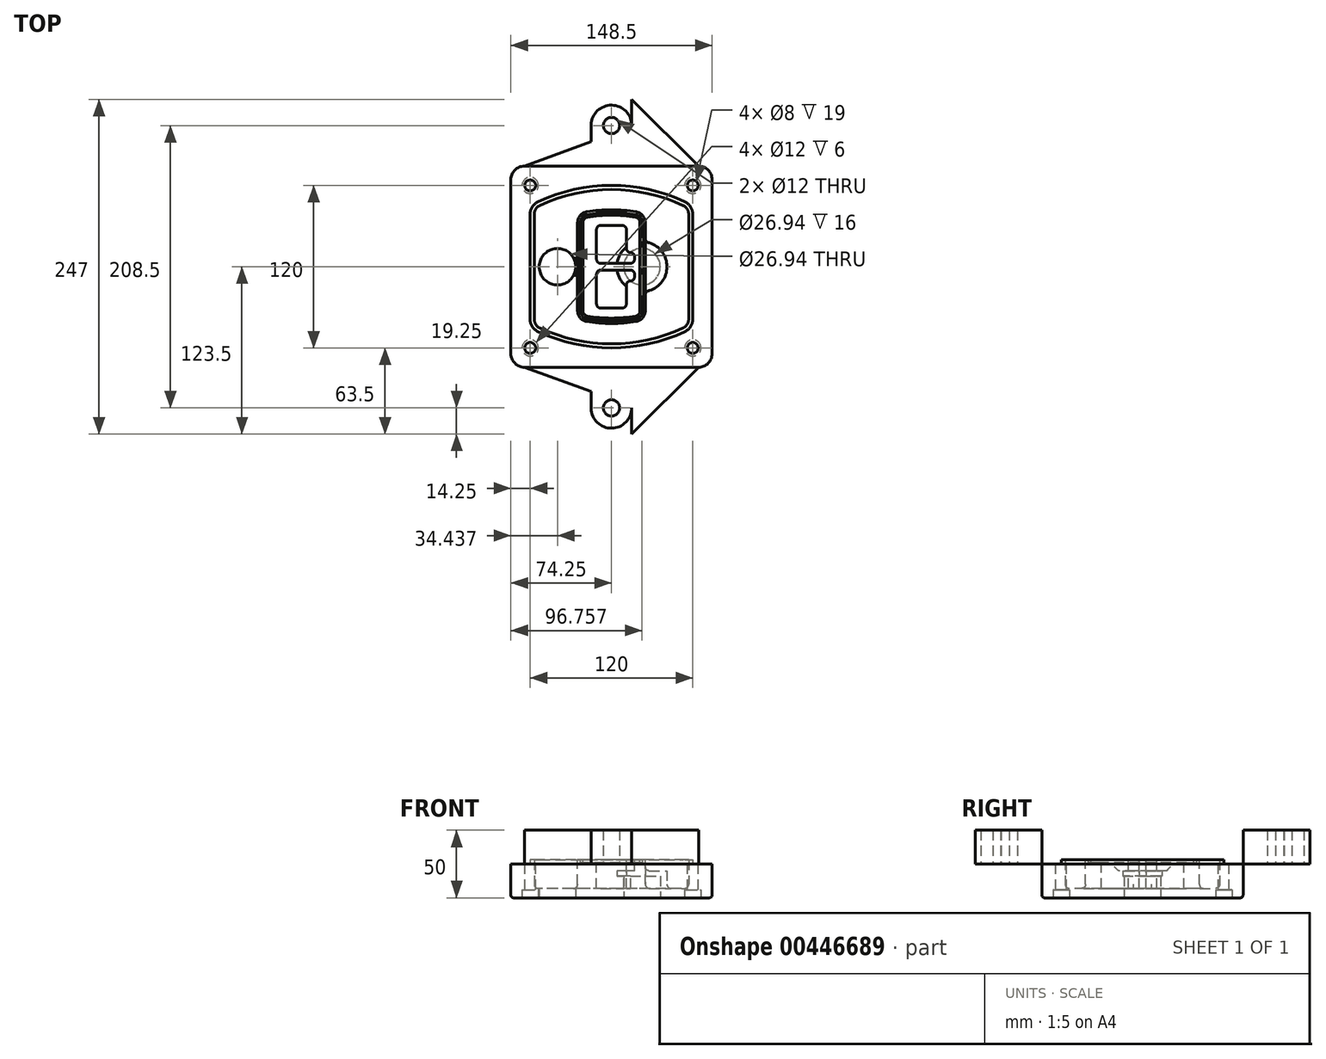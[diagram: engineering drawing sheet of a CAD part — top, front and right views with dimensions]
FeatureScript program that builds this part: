
annotation { "Feature Type Name" : "Feature", "Feature Type Description" : "" }
export const myFeature = defineFeature(function(context is Context, id is Id, definition is map)
    precondition{}
    {
        {
            var Q0;
            Q0=qCreatedBy(makeId("Top.planeOp"),FACE);
            var sketch = newSketch(context, id + "F0", { "sketchPlane" : qUnion([Q0])});
            skPoint(sketch, "E0.rect.middle", {"position": v(0, 0) * mm});
            skLineSegment(sketch, "E1.bottom", {"start": v(-64.25, -74.25) * mm, "end": v(64.25, -74.25) * mm});
            skLineSegment(sketch, "E1.top", {"start": v(-64.25, 74.25) * mm, "end": v(64.25, 74.25) * mm});
            skLineSegment(sketch, "E1.left", {"start": v(-74.25, -64.25) * mm, "end": v(-74.25, 64.25) * mm});
            skLineSegment(sketch, "E1.right", {"start": v(74.25, -64.25) * mm, "end": v(74.25, 64.25) * mm});
            skLineSegment(sketch, "E2", {"start": v(-74.25, 74.25) * mm, "end": v(74.25, -74.25) * mm, "construction": true});
            skLineSegment(sketch, "E3", {"start": v(74.25, 74.25) * mm, "end": v(-74.25, -74.25) * mm, "construction": true});
            skCircle(sketch, "E4", {"center": v(-60, 60) * mm, "radius": 4 * mm});
            skCircle(sketch, "E5", {"center": v(60, 60) * mm, "radius": 4 * mm});
            skCircle(sketch, "E6", {"center": v(60, -60) * mm, "radius": 4 * mm});
            skCircle(sketch, "E7", {"center": v(-60, -60) * mm, "radius": 4 * mm});
            skLineSegment(sketch, "E8", {"start": v(-60, 60) * mm, "end": v(60, 60) * mm, "construction": true});
            skLineSegment(sketch, "E9", {"start": v(60, 60) * mm, "end": v(60, -60) * mm, "construction": true});
            skLineSegment(sketch, "E10", {"start": v(60, -60) * mm, "end": v(-60, -60) * mm, "construction": true});
            skLineSegment(sketch, "E11", {"start": v(-60, -60) * mm, "end": v(-60, 60) * mm, "construction": true});
            skLineSegment(sketch, "E12", {"start": v(-60, 38.83) * mm, "end": v(-60, -38.83) * mm});
            skLineSegment(sketch, "E13", {"start": v(60, 38.83) * mm, "end": v(60, -38.83) * mm});
            skArc(sketch, "E14", {"start": v(54.26, 47.88) * mm, "mid": v(0, 60) * mm, "end": v(-54.26, 47.88) * mm});
            skArc(sketch, "E15", {"start": v(-54.26, -47.88) * mm, "mid": v(0, -60) * mm, "end": v(54.26, -47.88) * mm});
            skLineSegment(sketch, "E16", {"start": v(-60, 0) * mm, "end": v(60, 0) * mm, "construction": true});
            skPoint(sketch, "E17.visualSharp", {"position": v(-60, -45) * mm});
            skArc(sketch, "E17.filletArc", {"start": v(-60, -38.83) * mm, "mid": v(-58.44, -44.2) * mm, "end": v(-54.26, -47.88) * mm});
            skPoint(sketch, "E18.visualSharp", {"position": v(-60, 45) * mm});
            skArc(sketch, "E18.filletArc", {"start": v(-54.26, 47.88) * mm, "mid": v(-58.44, 44.2) * mm, "end": v(-60, 38.83) * mm});
            skPoint(sketch, "E19.visualSharp", {"position": v(60, 45) * mm});
            skArc(sketch, "E19.filletArc", {"start": v(60, 38.83) * mm, "mid": v(58.44, 44.2) * mm, "end": v(54.26, 47.88) * mm});
            skPoint(sketch, "E20.visualSharp", {"position": v(60, -45) * mm});
            skArc(sketch, "E20.filletArc", {"start": v(54.26, -47.88) * mm, "mid": v(58.44, -44.2) * mm, "end": v(60, -38.83) * mm});
            skPoint(sketch, "E21.visualSharp", {"position": v(-74.25, 74.25) * mm});
            skArc(sketch, "E21.filletArc", {"start": v(-64.25, 74.25) * mm, "mid": v(-71.32, 71.32) * mm, "end": v(-74.25, 64.25) * mm});
            skPoint(sketch, "E22.visualSharp", {"position": v(74.25, 74.25) * mm});
            skArc(sketch, "E22.filletArc", {"start": v(74.25, 64.25) * mm, "mid": v(71.32, 71.32) * mm, "end": v(64.25, 74.25) * mm});
            skPoint(sketch, "E23.visualSharp", {"position": v(74.25, -74.25) * mm});
            skArc(sketch, "E23.filletArc", {"start": v(64.25, -74.25) * mm, "mid": v(71.32, -71.32) * mm, "end": v(74.25, -64.25) * mm});
            skPoint(sketch, "E24.visualSharp", {"position": v(-74.25, -74.25) * mm});
            skArc(sketch, "E24.filletArc", {"start": v(-74.25, -64.25) * mm, "mid": v(-71.32, -71.32) * mm, "end": v(-64.25, -74.25) * mm});
            skArc(sketch, "E25.0", {"start": v(57, 38.83) * mm, "mid": v(55.9, 42.58) * mm, "end": v(52.98, 45.17) * mm});
            skLineSegment(sketch, "E25.1", {"start": v(57, 38.83) * mm, "end": v(57, -38.83) * mm});
            skArc(sketch, "E25.2", {"start": v(52.98, -45.17) * mm, "mid": v(55.9, -42.58) * mm, "end": v(57, -38.83) * mm});
            skArc(sketch, "E25.3", {"start": v(-52.98, -45.17) * mm, "mid": v(0, -57) * mm, "end": v(52.98, -45.17) * mm});
            skArc(sketch, "E25.4", {"start": v(-57, -38.83) * mm, "mid": v(-55.9, -42.58) * mm, "end": v(-52.98, -45.17) * mm});
            skArc(sketch, "E25.5", {"start": v(52.98, 45.17) * mm, "mid": v(0, 57) * mm, "end": v(-52.98, 45.17) * mm});
            skLineSegment(sketch, "E25.6", {"start": v(-57, 38.83) * mm, "end": v(-57, -38.83) * mm});
            skArc(sketch, "E25.7", {"start": v(-52.98, 45.17) * mm, "mid": v(-55.9, 42.58) * mm, "end": v(-57, 38.83) * mm});
            skArc(sketch, "E26.0", {"start": v(-55.96, 51.5) * mm, "mid": v(-61.82, 46.33) * mm, "end": v(-64, 38.83) * mm});
            skArc(sketch, "E26.1", {"start": v(55.96, 51.5) * mm, "mid": v(0, 64) * mm, "end": v(-55.96, 51.5) * mm});
            skArc(sketch, "E26.2", {"start": v(64, 38.83) * mm, "mid": v(61.82, 46.33) * mm, "end": v(55.96, 51.5) * mm});
            skLineSegment(sketch, "E26.3", {"start": v(64, 38.83) * mm, "end": v(64, -38.83) * mm});
            skArc(sketch, "E26.4", {"start": v(55.96, -51.5) * mm, "mid": v(61.82, -46.33) * mm, "end": v(64, -38.83) * mm});
            skLineSegment(sketch, "E26.5", {"start": v(-64, 38.83) * mm, "end": v(-64, -38.83) * mm});
            skArc(sketch, "E26.6", {"start": v(-55.96, -51.5) * mm, "mid": v(0, -64) * mm, "end": v(55.96, -51.5) * mm});
            skArc(sketch, "E26.7", {"start": v(-64, -38.83) * mm, "mid": v(-61.82, -46.33) * mm, "end": v(-55.96, -51.5) * mm});
            skSolve(sketch);
        }
        {
            var Q0;
            Q0=makeQuery(id+"F0.imprint","IMPRINT",FACE,{"disambiguationData":[TD([[makeQuery(id+"F0.imprint","IMPRINT",EDGE,{"derivedFrom":sQuery(id+"F0.wireOp",EDGE,"E1.bottom")}),1.0]])]});
            var Q1;
            Q1=makeQuery(id+"F0.imprint","IMPRINT",FACE,{"disambiguationData":[TD([[makeQuery(id+"F0.imprint","IMPRINT",EDGE,{"derivedFrom":sQuery(id+"F0.wireOp",EDGE,"E12")}),1.0]])]});
            var Q2;
            Q2=makeQuery(id+"F0.imprint","IMPRINT",FACE,{"disambiguationData":[TD([[makeQuery(id+"F0.imprint","IMPRINT",EDGE,{"derivedFrom":sQuery(id+"F0.wireOp",EDGE,"E25.0")}),1.0]])]});
            var Q3;
            Q3=makeQuery(id+"F0.imprint","IMPRINT",FACE,{"disambiguationData":[TD([[makeQuery(id+"F0.imprint","IMPRINT",EDGE,{"derivedFrom":sQuery(id+"F0.wireOp",EDGE,"E12")}),-1.0]])]});
            extrude(context, id + "F1", {"entities" : qUnion([Q0, Q1, Q2, Q3]), "oppositeDirection" : true, "depth" : 25 * mm});
        }
        {
            var Q0;
            Q0=makeQuery(id+"F0.imprint","IMPRINT",FACE,{"disambiguationData":[TD([[makeQuery(id+"F0.imprint","IMPRINT",EDGE,{"derivedFrom":sQuery(id+"F0.wireOp",EDGE,"E12")}),1.0]])]});
            extrude(context, id + "F2", {"entities" : qUnion([Q0]), "operationType" : NewBodyOperationType.ADD, "depth" : 3 * mm});
        }
        {
            var Q0;
            Q0=makeQuery(id+"F0.imprint","IMPRINT",FACE,{"disambiguationData":[TD([[makeQuery(id+"F0.imprint","IMPRINT",EDGE,{"derivedFrom":sQuery(id+"F0.wireOp",EDGE,"E25.0")}),1.0]])]});
            extrude(context, id + "F3", {"entities" : qUnion([Q0]), "operationType" : NewBodyOperationType.REMOVE, "oppositeDirection" : true, "depth" : 18 * mm});
        }
        {
            var Q0;
            Q0=makeQuery(id+"F2.opExtrude","CAP_FACE",FACE,{"disambiguationData":[OSD([sQuery(id+"F0.wireOp",EDGE,"E12"),sQuery(id+"F0.wireOp",EDGE,"E13"),sQuery(id+"F0.wireOp",EDGE,"E14"),sQuery(id+"F0.wireOp",EDGE,"E15"),sQuery(id+"F0.wireOp",EDGE,"E17.filletArc"),sQuery(id+"F0.wireOp",EDGE,"E18.filletArc"),sQuery(id+"F0.wireOp",EDGE,"E19.filletArc"),sQuery(id+"F0.wireOp",EDGE,"E20.filletArc"),sQuery(id+"F0.wireOp",EDGE,"E25.0"),sQuery(id+"F0.wireOp",EDGE,"E25.1"),sQuery(id+"F0.wireOp",EDGE,"E25.2"),sQuery(id+"F0.wireOp",EDGE,"E25.3"),sQuery(id+"F0.wireOp",EDGE,"E25.4"),sQuery(id+"F0.wireOp",EDGE,"E25.5"),sQuery(id+"F0.wireOp",EDGE,"E25.6"),sQuery(id+"F0.wireOp",EDGE,"E25.7")])],"isStart":false});
            var sketch = newSketch(context, id + "F4", { "sketchPlane" : qUnion([Q0])});
            skArc(sketch, "E27.0", {"start": v(-18.34, -40.45) * mm, "mid": v(0, -42) * mm, "end": v(18.34, -40.45) * mm});
            skArc(sketch, "E28.0", {"start": v(18.34, 40.45) * mm, "mid": v(0, 42) * mm, "end": v(-18.34, 40.45) * mm});
            skLineSegment(sketch, "E29", {"start": v(-25, 32.57) * mm, "end": v(-25, -32.57) * mm});
            skLineSegment(sketch, "E30", {"start": v(25, 32.57) * mm, "end": v(25, -32.57) * mm});
            skLineSegment(sketch, "E31", {"start": v(-25, 39.1) * mm, "end": v(25, 39.1) * mm, "construction": true});
            skLineSegment(sketch, "E32", {"start": v(-25, -39.1) * mm, "end": v(25, -39.1) * mm, "construction": true});
            skPoint(sketch, "E33.visualSharp", {"position": v(-25, 39.1) * mm});
            skArc(sketch, "E33.filletArc", {"start": v(-18.34, 40.45) * mm, "mid": v(-23.11, 37.73) * mm, "end": v(-25, 32.57) * mm});
            skPoint(sketch, "E34.visualSharp", {"position": v(25, 39.1) * mm});
            skArc(sketch, "E34.filletArc", {"start": v(25, 32.57) * mm, "mid": v(23.11, 37.73) * mm, "end": v(18.34, 40.45) * mm});
            skPoint(sketch, "E35.visualSharp", {"position": v(25, -39.1) * mm});
            skArc(sketch, "E35.filletArc", {"start": v(18.34, -40.45) * mm, "mid": v(23.11, -37.73) * mm, "end": v(25, -32.57) * mm});
            skPoint(sketch, "E36.visualSharp", {"position": v(-25, -39.1) * mm});
            skArc(sketch, "E36.filletArc", {"start": v(-25, -32.57) * mm, "mid": v(-23.11, -37.73) * mm, "end": v(-18.34, -40.45) * mm});
            skArc(sketch, "E37.0", {"start": v(52.98, 45.17) * mm, "mid": v(0, 57) * mm, "end": v(-52.98, 45.17) * mm});
            skArc(sketch, "E37.1", {"start": v(-52.98, 45.17) * mm, "mid": v(-55.9, 42.58) * mm, "end": v(-57, 38.83) * mm});
            skLineSegment(sketch, "E37.2", {"start": v(-57, 38.83) * mm, "end": v(-57, -38.83) * mm});
            skArc(sketch, "E37.3", {"start": v(-57, -38.83) * mm, "mid": v(-55.9, -42.58) * mm, "end": v(-52.98, -45.17) * mm});
            skArc(sketch, "E37.4", {"start": v(-52.98, -45.17) * mm, "mid": v(0, -57) * mm, "end": v(52.98, -45.17) * mm});
            skArc(sketch, "E37.5", {"start": v(52.98, -45.17) * mm, "mid": v(55.9, -42.58) * mm, "end": v(57, -38.83) * mm});
            skLineSegment(sketch, "E37.6", {"start": v(57, 38.83) * mm, "end": v(57, -38.83) * mm});
            skArc(sketch, "E37.7", {"start": v(57, 38.83) * mm, "mid": v(55.9, 42.58) * mm, "end": v(52.98, 45.17) * mm});
            skLineSegment(sketch, "E38.0", {"start": v(23, 32.57) * mm, "end": v(23, -32.57) * mm});
            skArc(sketch, "E38.1", {"start": v(18, -38.48) * mm, "mid": v(21.58, -36.44) * mm, "end": v(23, -32.57) * mm});
            skArc(sketch, "E38.2", {"start": v(-18, -38.48) * mm, "mid": v(0, -40) * mm, "end": v(18, -38.48) * mm});
            skArc(sketch, "E38.3", {"start": v(-23, -32.57) * mm, "mid": v(-21.58, -36.44) * mm, "end": v(-18, -38.48) * mm});
            skLineSegment(sketch, "E38.4", {"start": v(-23, 32.57) * mm, "end": v(-23, -32.57) * mm});
            skArc(sketch, "E38.5", {"start": v(23, 32.57) * mm, "mid": v(21.58, 36.44) * mm, "end": v(18, 38.48) * mm});
            skArc(sketch, "E38.6", {"start": v(-18, 38.48) * mm, "mid": v(-21.58, 36.44) * mm, "end": v(-23, 32.57) * mm});
            skArc(sketch, "E38.7", {"start": v(18, 38.48) * mm, "mid": v(0, 40) * mm, "end": v(-18, 38.48) * mm});
            skArc(sketch, "E39.0", {"start": v(21, 32.57) * mm, "mid": v(20.06, 35.15) * mm, "end": v(17.67, 36.5) * mm});
            skLineSegment(sketch, "E39.1", {"start": v(21, 32.57) * mm, "end": v(21, -32.57) * mm});
            skArc(sketch, "E39.2", {"start": v(17.67, -36.5) * mm, "mid": v(20.06, -35.15) * mm, "end": v(21, -32.57) * mm});
            skArc(sketch, "E39.3", {"start": v(-17.67, -36.5) * mm, "mid": v(0, -38) * mm, "end": v(17.67, -36.5) * mm});
            skArc(sketch, "E39.4", {"start": v(-21, -32.57) * mm, "mid": v(-20.06, -35.15) * mm, "end": v(-17.67, -36.5) * mm});
            skArc(sketch, "E39.5", {"start": v(17.67, 36.5) * mm, "mid": v(0, 38) * mm, "end": v(-17.67, 36.5) * mm});
            skLineSegment(sketch, "E39.6", {"start": v(-21, 32.57) * mm, "end": v(-21, -32.57) * mm});
            skArc(sketch, "E39.7", {"start": v(-17.67, 36.5) * mm, "mid": v(-20.06, 35.15) * mm, "end": v(-21, 32.57) * mm});
            skLineSegment(sketch, "E40", {"start": v(-25, 0) * mm, "end": v(25, 0) * mm, "construction": true});
            skLineSegment(sketch, "E41", {"start": v(-11, 5.5) * mm, "end": v(-11, 27.5) * mm});
            skLineSegment(sketch, "E42", {"start": v(-8, 30.5) * mm, "end": v(8, 30.5) * mm});
            skLineSegment(sketch, "E43", {"start": v(11, 27.5) * mm, "end": v(11, 13.5) * mm});
            skLineSegment(sketch, "E44", {"start": v(14, 10.5) * mm, "end": v(14, 10.5) * mm});
            skLineSegment(sketch, "E45", {"start": v(17, 7.5) * mm, "end": v(17, 5.5) * mm});
            skLineSegment(sketch, "E46", {"start": v(14, 2.5) * mm, "end": v(-8, 2.5) * mm});
            skPoint(sketch, "E47.visualSharp", {"position": v(-11, 30.5) * mm});
            skArc(sketch, "E47.filletArc", {"start": v(-8, 30.5) * mm, "mid": v(-10.12, 29.62) * mm, "end": v(-11, 27.5) * mm});
            skPoint(sketch, "E48.visualSharp", {"position": v(11, 30.5) * mm});
            skArc(sketch, "E48.filletArc", {"start": v(11, 27.5) * mm, "mid": v(10.12, 29.62) * mm, "end": v(8, 30.5) * mm});
            skPoint(sketch, "E49.visualSharp", {"position": v(11, 10.5) * mm});
            skArc(sketch, "E49.filletArc", {"start": v(11, 13.5) * mm, "mid": v(11.88, 11.38) * mm, "end": v(14, 10.5) * mm});
            skPoint(sketch, "E50.visualSharp", {"position": v(17, 10.5) * mm});
            skArc(sketch, "E50.filletArc", {"start": v(17, 7.5) * mm, "mid": v(16.12, 9.62) * mm, "end": v(14, 10.5) * mm});
            skPoint(sketch, "E51.visualSharp", {"position": v(17, 2.5) * mm});
            skArc(sketch, "E51.filletArc", {"start": v(14, 2.5) * mm, "mid": v(16.12, 3.38) * mm, "end": v(17, 5.5) * mm});
            skPoint(sketch, "E52.visualSharp", {"position": v(-11, 2.5) * mm});
            skArc(sketch, "E52.filletArc", {"start": v(-11, 5.5) * mm, "mid": v(-10.12, 3.38) * mm, "end": v(-8, 2.5) * mm});
            skLineSegment(sketch, "E53.0.MirrorCS", {"start": v(14, -2.5) * mm, "end": v(-8, -2.5) * mm});
            skArc(sketch, "E54.0.MirrorCS", {"start": v(-11, -5.5) * mm, "mid": v(-10.12, -3.38) * mm, "end": v(-8, -2.5) * mm});
            skLineSegment(sketch, "E55.0.MirrorCS", {"start": v(-11, -5.5) * mm, "end": v(-11, -27.5) * mm});
            skArc(sketch, "E56.0.MirrorCS", {"start": v(-8, -30.5) * mm, "mid": v(-10.12, -29.62) * mm, "end": v(-11, -27.5) * mm});
            skLineSegment(sketch, "E57.0.MirrorCS", {"start": v(-8, -30.5) * mm, "end": v(8, -30.5) * mm});
            skArc(sketch, "E58.0.MirrorCS", {"start": v(11, -27.5) * mm, "mid": v(10.12, -29.62) * mm, "end": v(8, -30.5) * mm});
            skLineSegment(sketch, "E59.0.MirrorCS", {"start": v(11, -27.5) * mm, "end": v(11, -13.5) * mm});
            skArc(sketch, "E60.0.MirrorCS", {"start": v(11, -13.5) * mm, "mid": v(11.88, -11.38) * mm, "end": v(14, -10.5) * mm});
            skArc(sketch, "E61.0.MirrorCS", {"start": v(17, -7.5) * mm, "mid": v(16.12, -9.62) * mm, "end": v(14, -10.5) * mm});
            skLineSegment(sketch, "E62.0.MirrorCS", {"start": v(17, -7.5) * mm, "end": v(17, -5.5) * mm});
            skArc(sketch, "E63.0.MirrorCS", {"start": v(14, -2.5) * mm, "mid": v(16.12, -3.38) * mm, "end": v(17, -5.5) * mm});
            skSolve(sketch);
        }
        {
            var Q0;
            Q0=makeQuery(id+"F4.imprint","IMPRINT",FACE,{"disambiguationData":[TD([[makeQuery(id+"F4.imprint","IMPRINT",EDGE,{"derivedFrom":sQuery(id+"F4.wireOp",EDGE,"E27.0")}),1.0]])]});
            var Q1;
            Q1=makeQuery(id+"F4.imprint","IMPRINT",FACE,{"disambiguationData":[TD([[makeQuery(id+"F4.imprint","IMPRINT",EDGE,{"derivedFrom":sQuery(id+"F4.wireOp",EDGE,"E38.0")}),-1.0]])]});
            var Q2;
            Q2=makeQuery(id+"F4.imprint","IMPRINT",FACE,{"disambiguationData":[TD([[makeQuery(id+"F4.imprint","IMPRINT",EDGE,{"derivedFrom":sQuery(id+"F4.wireOp",EDGE,"E39.0")}),1.0]])]});
            extrude(context, id + "F5", {"entities" : qUnion([Q0, Q1, Q2]), "operationType" : NewBodyOperationType.ADD, "endBound" : BoundingType.UP_TO_NEXT, "oppositeDirection" : true, "depth" : 25 * mm});
        }
        {
            var Q0;
            Q0=makeQuery(id+"F4.imprint","IMPRINT",FACE,{"disambiguationData":[TD([[makeQuery(id+"F4.imprint","IMPRINT",EDGE,{"derivedFrom":sQuery(id+"F4.wireOp",EDGE,"E38.0")}),-1.0]])]});
            extrude(context, id + "F6", {"entities" : qUnion([Q0]), "operationType" : NewBodyOperationType.REMOVE, "oppositeDirection" : true, "depth" : 2 * mm});
        }
        {
            var Q0;
            Q0=makeQuery(id+"F1.opExtrude","CAP_FACE",FACE,{"disambiguationData":[OSD([sQuery(id+"F0.wireOp",EDGE,"E1.bottom"),sQuery(id+"F0.wireOp",EDGE,"E1.top"),sQuery(id+"F0.wireOp",EDGE,"E1.left"),sQuery(id+"F0.wireOp",EDGE,"E1.right"),sQuery(id+"F0.wireOp",EDGE,"E4"),sQuery(id+"F0.wireOp",EDGE,"E5"),sQuery(id+"F0.wireOp",EDGE,"E6"),sQuery(id+"F0.wireOp",EDGE,"E7"),sQuery(id+"F0.wireOp",EDGE,"E21.filletArc"),sQuery(id+"F0.wireOp",EDGE,"E22.filletArc"),sQuery(id+"F0.wireOp",EDGE,"E23.filletArc"),sQuery(id+"F0.wireOp",EDGE,"E24.filletArc")])],"isStart":false});
            var sketch = newSketch(context, id + "F7", { "sketchPlane" : qUnion([Q0])});
            skCircle(sketch, "E64", {"center": v(22.5, 0) * mm, "radius": 13.47 * mm});
            skCircle(sketch, "E65", {"center": v(-39.81, 0) * mm, "radius": 13.47 * mm});
            skLineSegment(sketch, "E66", {"start": v(74.25, 0) * mm, "end": v(-74.25, 0) * mm});
            skCircle(sketch, "E67", {"center": v(22.5, 0) * mm, "radius": 18.47 * mm});
            skCircle(sketch, "E68", {"center": v(60, -60) * mm, "radius": 6 * mm});
            skCircle(sketch, "E69", {"center": v(-60, -60) * mm, "radius": 6 * mm});
            skCircle(sketch, "E70", {"center": v(-60, 60) * mm, "radius": 6 * mm});
            skCircle(sketch, "E71", {"center": v(60, 60) * mm, "radius": 6 * mm});
            skSolve(sketch);
        }
        {
            var Q0;
            {var subQ1=sQuery(id+"F7.wireOp",EDGE,"E66");var subQ4=sQuery(id+"F7.wireOp",EDGE,"E64");var subQ6=makeQuery(id+"F7.imprint","INTERSECT",VERTEX,{"disambiguationData":[OD(0.0)],"derivedFrom":[subQ4,subQ1]});Q0=makeQuery(id+"F7.imprint","IMPRINT",FACE,{"disambiguationData":[TD([[makeQuery(id+"F7.imprint","IMPRINT",EDGE,{"disambiguationData":[TD([[subQ6,-1.0]])],"derivedFrom":subQ4}),-1.0]])]});}
            var Q1;
            {var subQ0=sQuery(id+"F7.wireOp",EDGE,"E66");var subQ1=sQuery(id+"F7.wireOp",EDGE,"E64");var subQ3=makeQuery(id+"F7.imprint","INTERSECT",VERTEX,{"disambiguationData":[OD(0.0)],"derivedFrom":[subQ1,subQ0]});Q1=makeQuery(id+"F7.imprint","IMPRINT",FACE,{"disambiguationData":[TD([[makeQuery(id+"F7.imprint","IMPRINT",EDGE,{"disambiguationData":[TD([[subQ3,-1.0]])],"derivedFrom":subQ1}),1.0]])]});}
            var Q2;
            {var subQ0=sQuery(id+"F7.wireOp",EDGE,"E66");var subQ1=sQuery(id+"F7.wireOp",EDGE,"E64");var subQ3=makeQuery(id+"F7.imprint","INTERSECT",VERTEX,{"disambiguationData":[OD(0.0)],"derivedFrom":[subQ1,subQ0]});Q2=makeQuery(id+"F7.imprint","IMPRINT",FACE,{"disambiguationData":[TD([[makeQuery(id+"F7.imprint","IMPRINT",EDGE,{"disambiguationData":[TD([[subQ3,1.0]])],"derivedFrom":subQ1}),1.0]])]});}
            var Q3;
            {var subQ1=sQuery(id+"F7.wireOp",EDGE,"E66");var subQ4=sQuery(id+"F7.wireOp",EDGE,"E64");var subQ6=makeQuery(id+"F7.imprint","INTERSECT",VERTEX,{"disambiguationData":[OD(0.0)],"derivedFrom":[subQ4,subQ1]});Q3=makeQuery(id+"F7.imprint","IMPRINT",FACE,{"disambiguationData":[TD([[makeQuery(id+"F7.imprint","IMPRINT",EDGE,{"disambiguationData":[TD([[subQ6,1.0]])],"derivedFrom":subQ4}),-1.0]])]});}
            extrude(context, id + "F8", {"entities" : qUnion([Q0, Q1, Q2, Q3]), "operationType" : NewBodyOperationType.ADD, "oppositeDirection" : true, "depth" : 20 * mm});
        }
        {
            var Q0;
            {var subQ0=sQuery(id+"F7.wireOp",EDGE,"E66");var subQ1=sQuery(id+"F7.wireOp",EDGE,"E64");var subQ3=makeQuery(id+"F7.imprint","INTERSECT",VERTEX,{"disambiguationData":[OD(0.0)],"derivedFrom":[subQ1,subQ0]});Q0=makeQuery(id+"F7.imprint","IMPRINT",FACE,{"disambiguationData":[TD([[makeQuery(id+"F7.imprint","IMPRINT",EDGE,{"disambiguationData":[TD([[subQ3,-1.0]])],"derivedFrom":subQ1}),1.0]])]});}
            var Q1;
            {var subQ0=sQuery(id+"F7.wireOp",EDGE,"E66");var subQ1=sQuery(id+"F7.wireOp",EDGE,"E64");var subQ3=makeQuery(id+"F7.imprint","INTERSECT",VERTEX,{"disambiguationData":[OD(0.0)],"derivedFrom":[subQ1,subQ0]});Q1=makeQuery(id+"F7.imprint","IMPRINT",FACE,{"disambiguationData":[TD([[makeQuery(id+"F7.imprint","IMPRINT",EDGE,{"disambiguationData":[TD([[subQ3,1.0]])],"derivedFrom":subQ1}),1.0]])]});}
            extrude(context, id + "F9", {"entities" : qUnion([Q0, Q1]), "operationType" : NewBodyOperationType.REMOVE, "oppositeDirection" : true, "depth" : 16 * mm});
        }
        {
            var Q0;
            {var subQ0=sQuery(id+"F7.wireOp",EDGE,"E66");var subQ1=sQuery(id+"F7.wireOp",EDGE,"E65");var subQ3=makeQuery(id+"F7.imprint","INTERSECT",VERTEX,{"disambiguationData":[OD(0.0)],"derivedFrom":[subQ1,subQ0]});Q0=makeQuery(id+"F7.imprint","IMPRINT",FACE,{"disambiguationData":[TD([[makeQuery(id+"F7.imprint","IMPRINT",EDGE,{"disambiguationData":[TD([[subQ3,-1.0]])],"derivedFrom":subQ1}),1.0]])]});}
            var Q1;
            {var subQ0=sQuery(id+"F7.wireOp",EDGE,"E66");var subQ1=sQuery(id+"F7.wireOp",EDGE,"E65");var subQ3=makeQuery(id+"F7.imprint","INTERSECT",VERTEX,{"disambiguationData":[OD(0.0)],"derivedFrom":[subQ1,subQ0]});Q1=makeQuery(id+"F7.imprint","IMPRINT",FACE,{"disambiguationData":[TD([[makeQuery(id+"F7.imprint","IMPRINT",EDGE,{"disambiguationData":[TD([[subQ3,1.0]])],"derivedFrom":subQ1}),1.0]])]});}
            extrude(context, id + "F10", {"entities" : qUnion([Q0, Q1]), "operationType" : NewBodyOperationType.REMOVE, "oppositeDirection" : true, "depth" : 25 * mm});
        }
        {
            var Q0;
            Q0=makeQuery(id+"F7.imprint","IMPRINT",FACE,{"disambiguationData":[TD([[makeQuery(id+"F7.imprint","IMPRINT",EDGE,{"derivedFrom":sQuery(id+"F7.wireOp",EDGE,"E68")}),1.0]])]});
            var Q1;
            Q1=makeQuery(id+"F7.imprint","IMPRINT",FACE,{"disambiguationData":[TD([[makeQuery(id+"F7.imprint","IMPRINT",EDGE,{"derivedFrom":makeQuery(id+"F1.opExtrude","CAP_EDGE",EDGE,{"disambiguationData":[OSD([sQuery(id+"F0.wireOp",EDGE,"E5")])],"isStart":false})}),-1.0]])]});
            var Q2;
            Q2=makeQuery(id+"F7.imprint","IMPRINT",FACE,{"disambiguationData":[TD([[makeQuery(id+"F7.imprint","IMPRINT",EDGE,{"derivedFrom":sQuery(id+"F7.wireOp",EDGE,"E69")}),1.0]])]});
            var Q3;
            Q3=makeQuery(id+"F7.imprint","IMPRINT",FACE,{"disambiguationData":[TD([[makeQuery(id+"F7.imprint","IMPRINT",EDGE,{"derivedFrom":makeQuery(id+"F1.opExtrude","CAP_EDGE",EDGE,{"disambiguationData":[OSD([sQuery(id+"F0.wireOp",EDGE,"E4")])],"isStart":false})}),-1.0]])]});
            var Q4;
            Q4=makeQuery(id+"F7.imprint","IMPRINT",FACE,{"disambiguationData":[TD([[makeQuery(id+"F7.imprint","IMPRINT",EDGE,{"derivedFrom":sQuery(id+"F7.wireOp",EDGE,"E70")}),1.0]])]});
            var Q5;
            Q5=makeQuery(id+"F7.imprint","IMPRINT",FACE,{"disambiguationData":[TD([[makeQuery(id+"F7.imprint","IMPRINT",EDGE,{"derivedFrom":makeQuery(id+"F1.opExtrude","CAP_EDGE",EDGE,{"disambiguationData":[OSD([sQuery(id+"F0.wireOp",EDGE,"E7")])],"isStart":false})}),-1.0]])]});
            var Q6;
            Q6=makeQuery(id+"F7.imprint","IMPRINT",FACE,{"disambiguationData":[TD([[makeQuery(id+"F7.imprint","IMPRINT",EDGE,{"derivedFrom":sQuery(id+"F7.wireOp",EDGE,"E71")}),1.0]])]});
            var Q7;
            Q7=makeQuery(id+"F7.imprint","IMPRINT",FACE,{"disambiguationData":[TD([[makeQuery(id+"F7.imprint","IMPRINT",EDGE,{"derivedFrom":makeQuery(id+"F1.opExtrude","CAP_EDGE",EDGE,{"disambiguationData":[OSD([sQuery(id+"F0.wireOp",EDGE,"E6")])],"isStart":false})}),-1.0]])]});
            extrude(context, id + "F11", {"entities" : qUnion([Q0, Q1, Q2, Q3, Q4, Q5, Q6, Q7]), "operationType" : NewBodyOperationType.REMOVE, "oppositeDirection" : true, "depth" : 6 * mm});
        }
        {
            var Q0;
            Q0=makeQuery(id+"F9.boolean.opBoolean","COPY",FACE,{"derivedFrom":makeQuery(id+"F9.opExtrude","CAP_FACE",FACE,{"disambiguationData":[OSD([sQuery(id+"F7.wireOp",EDGE,"E64")])],"isStart":false})});
            var sketch = newSketch(context, id + "F12", { "sketchPlane" : qUnion([Q0])});
            skArc(sketch, "E72.0", {"start": v(11, 14.45) * mm, "mid": v(6.45, 9.13) * mm, "end": v(4.2, 2.5) * mm});
            skArc(sketch, "E72.1", {"start": v(4.2, -2.5) * mm, "mid": v(6.45, -9.13) * mm, "end": v(11, -14.45) * mm});
            skLineSegment(sketch, "E73", {"start": v(4.2, -2.5) * mm, "end": v(14, -2.5) * mm});
            skLineSegment(sketch, "E74.0", {"start": v(14, 2.5) * mm, "end": v(4.2, 2.5) * mm});
            skArc(sketch, "E74.1", {"start": v(14, 2.5) * mm, "mid": v(16.12, 3.38) * mm, "end": v(17, 5.5) * mm});
            skLineSegment(sketch, "E74.2", {"start": v(17, 7.5) * mm, "end": v(17, 5.5) * mm});
            skArc(sketch, "E74.3", {"start": v(17, 7.5) * mm, "mid": v(16.12, 9.62) * mm, "end": v(14, 10.5) * mm});
            skArc(sketch, "E74.4", {"start": v(11, 13.5) * mm, "mid": v(11.88, 11.38) * mm, "end": v(14, 10.5) * mm});
            skLineSegment(sketch, "E74.5", {"start": v(11, 14.45) * mm, "end": v(11, 13.5) * mm});
            skLineSegment(sketch, "E74.7", {"start": v(14, -2.5) * mm, "end": v(4.2, -2.5) * mm});
            skArc(sketch, "E74.8", {"start": v(14, -2.5) * mm, "mid": v(16.12, -3.38) * mm, "end": v(17, -5.5) * mm});
            skLineSegment(sketch, "E74.9", {"start": v(17, -7.5) * mm, "end": v(17, -5.5) * mm});
            skArc(sketch, "E74.10", {"start": v(17, -7.5) * mm, "mid": v(16.12, -9.62) * mm, "end": v(14, -10.5) * mm});
            skArc(sketch, "E74.11", {"start": v(11, -13.5) * mm, "mid": v(11.88, -11.38) * mm, "end": v(14, -10.5) * mm});
            skLineSegment(sketch, "E74.12", {"start": v(11, -14.45) * mm, "end": v(11, -13.5) * mm});
            skPoint(sketch, "E75.orphan", {"position": v(11, -27.5) * mm});
            skPoint(sketch, "E76.orphan", {"position": v(-8, -2.5) * mm});
            skPoint(sketch, "E77.orphan", {"position": v(-8, 2.5) * mm});
            skPoint(sketch, "E78.orphan", {"position": v(11, 27.5) * mm});
            skSolve(sketch);
        }
        {
            var Q0;
            {var subQ7=sQuery(id+"F12.wireOp",EDGE,"E72.0");var subQ14=sQuery(id+"F12.wireOp",EDGE,"E72.1");var subQ16=sQuery(id+"F12.wireOp",EDGE,"E74.1");var subQ18=sQuery(id+"F12.wireOp",EDGE,"E74.8");Q0=qUnion([makeQuery(id+"F12.imprint","IMPRINT",FACE,{"disambiguationData":[TD([[makeQuery(id+"F12.imprint","IMPRINT",EDGE,{"derivedFrom":subQ7}),1.0]])]}),makeQuery(id+"F12.imprint","IMPRINT",FACE,{"disambiguationData":[TD([[makeQuery(id+"F12.imprint","IMPRINT",EDGE,{"derivedFrom":subQ14}),1.0]])]}),makeQuery(id+"F12.imprint","IMPRINT",FACE,{"disambiguationData":[TD([[makeQuery(id+"F12.imprint","IMPRINT",EDGE,{"derivedFrom":subQ16}),1.0]])]}),makeQuery(id+"F12.imprint","IMPRINT",FACE,{"disambiguationData":[TD([[makeQuery(id+"F12.imprint","IMPRINT",EDGE,{"derivedFrom":subQ18}),-1.0]])]})]);}
            var Q1;
            Q1=makeQuery(id+"F5.boolean.opBoolean","SPLIT",FACE,{"disambiguationData":[TD([makeQuery(id+"F5.opExtrude","SWEPT_FACE",FACE,{"disambiguationData":[OSD([sQuery(id+"F4.wireOp",EDGE,"E41")])]})])],"derivedFrom":makeQuery(id+"F3.boolean.opBoolean","COPY",FACE,{"derivedFrom":makeQuery(id+"F3.opExtrude","CAP_FACE",FACE,{"disambiguationData":[OSD([sQuery(id+"F0.wireOp",EDGE,"E25.0"),sQuery(id+"F0.wireOp",EDGE,"E25.1"),sQuery(id+"F0.wireOp",EDGE,"E25.2"),sQuery(id+"F0.wireOp",EDGE,"E25.3"),sQuery(id+"F0.wireOp",EDGE,"E25.4"),sQuery(id+"F0.wireOp",EDGE,"E25.5"),sQuery(id+"F0.wireOp",EDGE,"E25.6"),sQuery(id+"F0.wireOp",EDGE,"E25.7")])],"isStart":false})})});
            extrude(context, id + "F13", {"entities" : qUnion([Q0]), "operationType" : NewBodyOperationType.REMOVE, "endBound" : BoundingType.UP_TO_SURFACE, "endBoundEntityFace" : qUnion([Q1]), "depth" : 25 * mm});
        }
        {
            var Q0;
            Q0=makeQuery(id+"F3.boolean.opBoolean","COPY",EDGE,{"derivedFrom":makeQuery(id+"F3.opExtrude","CAP_EDGE",EDGE,{"disambiguationData":[OSD([sQuery(id+"F0.wireOp",EDGE,"E25.6")])],"isStart":false})});
            var Q1;
            Q1=makeQuery(id+"F8.boolean.opBoolean","INTERSECT",EDGE,{"derivedFrom":[makeQuery(id+"F5.opExtrude","SWEPT_FACE",FACE,{"disambiguationData":[OSD([sQuery(id+"F4.wireOp",EDGE,"E30")])]}),makeQuery(id+"F8.opExtrude","CAP_FACE",FACE,{"disambiguationData":[OSD([sQuery(id+"F7.wireOp",EDGE,"E67")])],"isStart":false})]});
            var Q2;
            Q2=makeQuery(id+"F8.boolean.opBoolean","INTERSECT",EDGE,{"disambiguationData":[OD(1.0)],"derivedFrom":[makeQuery(id+"F5.opExtrude","SWEPT_FACE",FACE,{"disambiguationData":[OSD([sQuery(id+"F4.wireOp",EDGE,"E30")])]}),makeQuery(id+"F8.opExtrude","SWEPT_FACE",FACE,{"disambiguationData":[OSD([sQuery(id+"F7.wireOp",EDGE,"E67")])]})]});
            var Q3;
            {var subQ0=sQuery(id+"F4.wireOp",EDGE,"E30");Q3=makeQuery(id+"F8.boolean.opBoolean","SPLIT",EDGE,{"disambiguationData":[TD([makeQuery(id+"F5.opExtrude","SWEPT_FACE",FACE,{"disambiguationData":[OSD([sQuery(id+"F4.wireOp",EDGE,"E35.filletArc")])]})])],"derivedFrom":makeQuery(id+"F5.opExtrude","CAP_EDGE",EDGE,{"disambiguationData":[OSD([subQ0])],"isStart":false})});}
            var Q4;
            {var subQ0=sQuery(id+"F0.wireOp",EDGE,"E25.7");var subQ1=sQuery(id+"F0.wireOp",EDGE,"E25.1");var subQ2=sQuery(id+"F0.wireOp",EDGE,"E25.6");var subQ3=sQuery(id+"F0.wireOp",EDGE,"E25.5");var subQ4=sQuery(id+"F0.wireOp",EDGE,"E25.4");var subQ5=sQuery(id+"F0.wireOp",EDGE,"E25.0");var subQ6=sQuery(id+"F0.wireOp",EDGE,"E25.2");var subQ7=sQuery(id+"F0.wireOp",EDGE,"E25.3");Q4=makeQuery(id+"F8.boolean.opBoolean","INTERSECT",EDGE,{"derivedFrom":[makeQuery(id+"F5.boolean.opBoolean","SPLIT",FACE,{"disambiguationData":[TD([makeQuery(id+"F2.opExtrude","SWEPT_FACE",FACE,{"disambiguationData":[OSD([subQ5])]})])],"derivedFrom":makeQuery(id+"F3.boolean.opBoolean","COPY",FACE,{"derivedFrom":makeQuery(id+"F3.opExtrude","CAP_FACE",FACE,{"disambiguationData":[OSD([subQ5,subQ1,subQ6,subQ7,subQ4,subQ3,subQ2,subQ0])],"isStart":false})})}),makeQuery(id+"F8.opExtrude","SWEPT_FACE",FACE,{"disambiguationData":[OSD([sQuery(id+"F7.wireOp",EDGE,"E67")])]})]});}
            var Q5;
            Q5=makeQuery(id+"F8.boolean.opBoolean","INTERSECT",EDGE,{"disambiguationData":[OD(0.0)],"derivedFrom":[makeQuery(id+"F5.opExtrude","SWEPT_FACE",FACE,{"disambiguationData":[OSD([sQuery(id+"F4.wireOp",EDGE,"E30")])]}),makeQuery(id+"F8.opExtrude","SWEPT_FACE",FACE,{"disambiguationData":[OSD([sQuery(id+"F7.wireOp",EDGE,"E67")])]})]});
            fillet(context, id + "F14", {"entities" : qUnion([Q0, Q1, Q2, Q3, Q4, Q5]), "radius" : 3 * mm, "tangentPropagation" : true, "allowEdgeOverflow" : false});
        }
        {
            var Q0;
            Q0=makeQuery(id+"F1.opExtrude","CAP_EDGE",EDGE,{"disambiguationData":[OSD([sQuery(id+"F0.wireOp",EDGE,"E1.bottom")])],"isStart":false});
            fillet(context, id + "F15", {"entities" : qUnion([Q0]), "radius" : 2 * mm, "tangentPropagation" : true, "allowEdgeOverflow" : false});
        }
        {
            var Q0;
            {var subQ0=sQuery(id+"F0.wireOp",EDGE,"E21.filletArc");var subQ1=sQuery(id+"F0.wireOp",EDGE,"E7");var subQ2=sQuery(id+"F0.wireOp",EDGE,"E6");var subQ3=sQuery(id+"F0.wireOp",EDGE,"E5");var subQ4=sQuery(id+"F0.wireOp",EDGE,"E4");var subQ5=sQuery(id+"F0.wireOp",EDGE,"E22.filletArc");var subQ6=sQuery(id+"F0.wireOp",EDGE,"E1.bottom");var subQ7=sQuery(id+"F0.wireOp",EDGE,"E1.right");var subQ8=sQuery(id+"F0.wireOp",EDGE,"E1.top");var subQ9=sQuery(id+"F0.wireOp",EDGE,"E1.left");var subQ10=sQuery(id+"F0.wireOp",EDGE,"E23.filletArc");var subQ11=sQuery(id+"F0.wireOp",EDGE,"E24.filletArc");Q0=makeQuery(id+"F2.boolean.opBoolean","SPLIT",FACE,{"disambiguationData":[TD([makeQuery(id+"F1.opExtrude","SWEPT_FACE",FACE,{"disambiguationData":[OSD([subQ6])]})])],"derivedFrom":makeQuery(id+"F1.opExtrude","CAP_FACE",FACE,{"disambiguationData":[OSD([subQ6,subQ8,subQ9,subQ7,subQ4,subQ3,subQ2,subQ1,subQ0,subQ5,subQ10,subQ11])],"isStart":true})});}
            var sketch = newSketch(context, id + "F16", { "sketchPlane" : qUnion([Q0])});
            skCircle(sketch, "E79", {"center": v(0, 104.25) * mm, "radius": 6 * mm});
            skArc(sketch, "E80", {"start": v(-15, 104.68) * mm, "mid": v(0.21, 119.25) * mm, "end": v(15, 104.25) * mm});
            skLineSegment(sketch, "E81", {"start": v(0, 104.25) * mm, "end": v(0, 74.25) * mm});
            skLineSegment(sketch, "E82", {"start": v(0, 74.25) * mm, "end": v(0, 74.25) * mm});
            skLineSegment(sketch, "E83", {"start": v(15, 123.5) * mm, "end": v(15, 104.25) * mm});
            skLineSegment(sketch, "E84", {"start": v(-15, 104.68) * mm, "end": v(-15, 92.25) * mm});
            skLineSegment(sketch, "E85", {"start": v(-64.25, 74.25) * mm, "end": v(-15, 92.25) * mm});
            skLineSegment(sketch, "E86", {"start": v(15, 123.5) * mm, "end": v(64.25, 74.25) * mm});
            skLineSegment(sketch, "E87", {"start": v(-54.01, 74.25) * mm, "end": v(-64.25, 74.25) * mm});
            skLineSegment(sketch, "E88", {"start": v(64.25, 74.25) * mm, "end": v(-64.25, 74.25) * mm});
            skLineSegment(sketch, "E89", {"start": v(-93.68, 0) * mm, "end": v(88.95, 0) * mm});
            skLineSegment(sketch, "E90.MirrorCS", {"start": v(-64.25, -74.25) * mm, "end": v(-15, -92.25) * mm});
            skLineSegment(sketch, "E91.MirrorCS", {"start": v(-15, -104.68) * mm, "end": v(-15, -92.25) * mm});
            skArc(sketch, "E92.MirrorCS", {"start": v(-15, -104.68) * mm, "mid": v(0.21, -119.25) * mm, "end": v(15, -104.25) * mm});
            skLineSegment(sketch, "E93.MirrorCS", {"start": v(64.25, -74.25) * mm, "end": v(-64.25, -74.25) * mm});
            skLineSegment(sketch, "E94.MirrorCS", {"start": v(15, -123.5) * mm, "end": v(64.25, -74.25) * mm});
            skLineSegment(sketch, "E95.MirrorCS", {"start": v(15, -123.5) * mm, "end": v(15, -104.25) * mm});
            skCircle(sketch, "E96.MirrorC", {"center": v(0, -104.25) * mm, "radius": 6 * mm});
            skLineSegment(sketch, "E97.MirrorCS", {"start": v(0, -104.25) * mm, "end": v(0, -74.25) * mm});
            skSolve(sketch);
        }
        {
            var Q0;
            Q0=makeQuery(id+"F16.imprint","IMPRINT",FACE,{"disambiguationData":[TD([[makeQuery(id+"F16.imprint","IMPRINT",EDGE,{"derivedFrom":sQuery(id+"F16.wireOp",EDGE,"E92.MirrorCS")}),1.0]])]});
            var Q1;
            Q1=makeQuery(id+"F16.imprint","IMPRINT",FACE,{"disambiguationData":[TD([[makeQuery(id+"F16.imprint","IMPRINT",EDGE,{"derivedFrom":sQuery(id+"F16.wireOp",EDGE,"E79")}),-1.0]])]});
            extrude(context, id + "F17", {"entities" : qUnion([Q0, Q1]), "depth" : 25 * mm});
        }
    });
